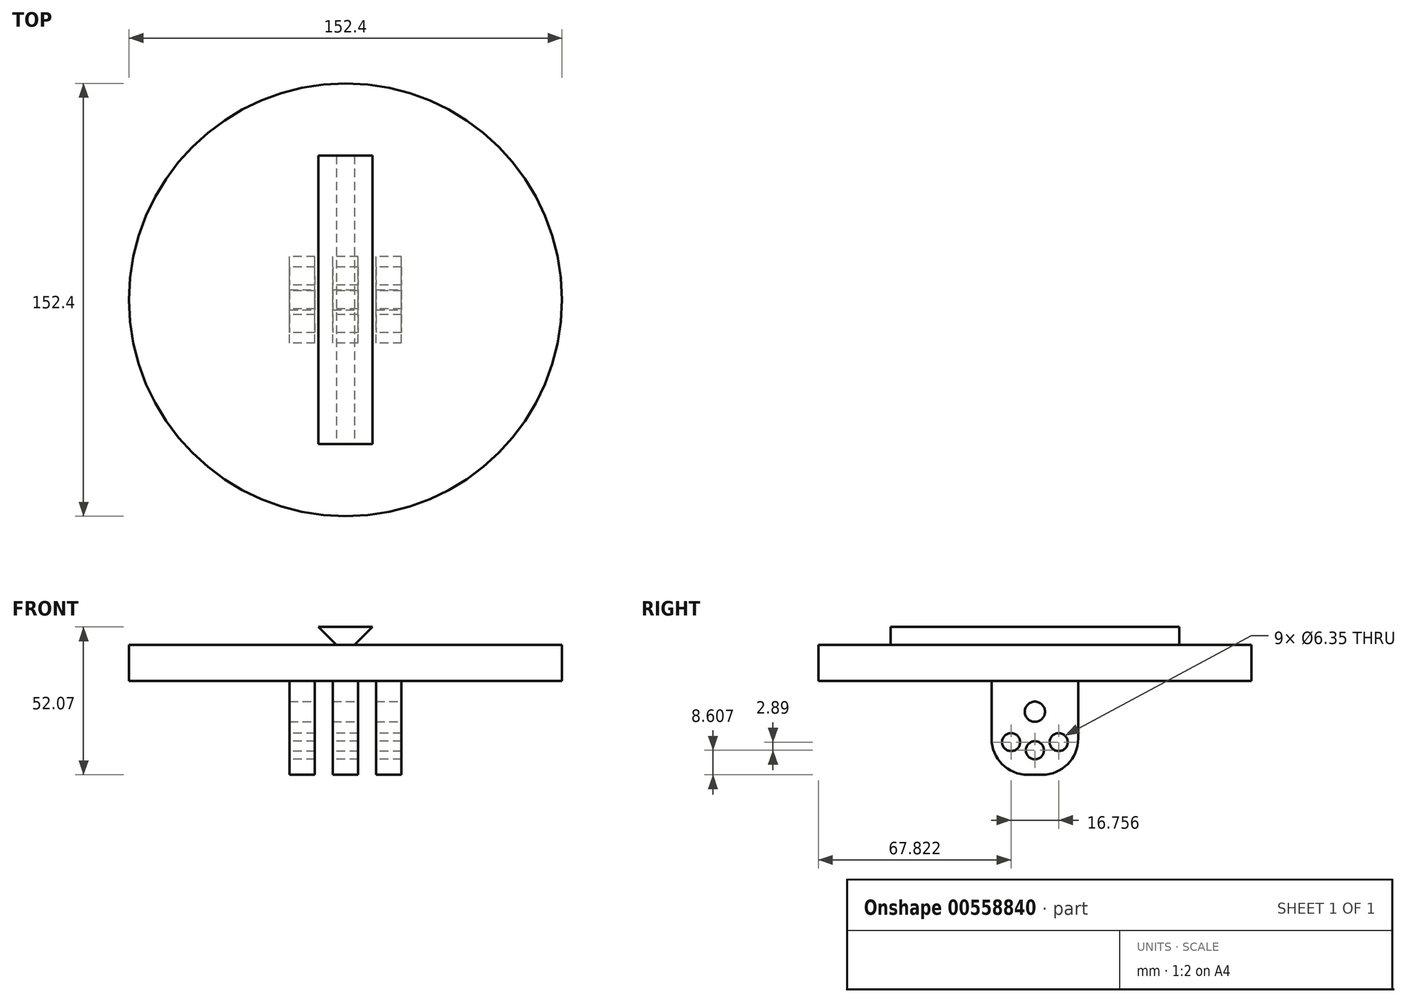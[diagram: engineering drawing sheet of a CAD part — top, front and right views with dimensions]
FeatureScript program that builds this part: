
annotation { "Feature Type Name" : "Feature", "Feature Type Description" : "" }
export const myFeature = defineFeature(function(context is Context, id is Id, definition is map)
    precondition{}
    {
        {
            var Q0;
            Q0=qCreatedBy(makeId("Top.planeOp"),FACE);
            var sketch = newSketch(context, id + "F0", { "sketchPlane" : qUnion([Q0])});
            skCircle(sketch, "E0", {"center": v(0, 0) * mm, "radius": 76.2 * mm});
            skSolve(sketch);
        }
        {
            var Q0;
            Q0=makeQuery(id+"F0.imprint","IMPRINT",FACE,{"disambiguationData":[TD([[makeQuery(id+"F0.imprint","IMPRINT",EDGE,{"derivedFrom":sQuery(id+"F0.wireOp",EDGE,"E0")}),1.0]])]});
            extrude(context, id + "F1", {"entities" : qUnion([Q0]), "depth" : 12.7 * mm, "offsetDistance" : 25.4 * mm});
        }
        {
            var Q0;
            Q0=makeQuery(id+"F1.opExtrude","CAP_FACE",FACE,{"disambiguationData":[OSD([sQuery(id+"F0.wireOp",EDGE,"E0")])],"isStart":false});
            var sketch = newSketch(context, id + "F2", { "sketchPlane" : qUnion([Q0])});
            skLineSegment(sketch, "E1.bottom", {"start": v(-9.53, 50.8) * mm, "end": v(9.53, 50.8) * mm});
            skLineSegment(sketch, "E1.top", {"start": v(-9.53, -50.8) * mm, "end": v(9.52, -50.8) * mm});
            skLineSegment(sketch, "E1.left", {"start": v(-9.53, 50.8) * mm, "end": v(-9.53, -50.8) * mm});
            skLineSegment(sketch, "E1.right", {"start": v(9.53, 50.8) * mm, "end": v(9.52, -50.8) * mm});
            skPoint(sketch, "E1.middle", {"position": v(0, 0) * mm});
            skSolve(sketch);
        }
        {
            var Q0;
            Q0=makeQuery(id+"F2.imprint","IMPRINT",FACE,{"disambiguationData":[TD([[makeQuery(id+"F2.imprint","IMPRINT",EDGE,{"derivedFrom":sQuery(id+"F2.wireOp",EDGE,"E1.bottom")}),-1.0]])]});
            extrude(context, id + "F3", {"entities" : qUnion([Q0]), "operationType" : NewBodyOperationType.ADD, "depth" : 6.35 * mm, "offsetDistance" : 25.4 * mm});
        }
        {
            var Q0;
            Q0=makeQuery(id+"F3.opExtrude","SWEPT_FACE",FACE,{"disambiguationData":[OSD([sQuery(id+"F2.wireOp",EDGE,"E1.top")])]});
            var sketch = newSketch(context, id + "F4", { "sketchPlane" : qUnion([Q0])});
            skLineSegment(sketch, "E2", {"start": v(-9.53, 19.05) * mm, "end": v(-3.18, 12.7) * mm});
            skLineSegment(sketch, "E3", {"start": v(9.52, 19.05) * mm, "end": v(3.17, 12.7) * mm});
            skSolve(sketch);
        }
        {
            var Q0;
            Q0 = qSketchRegion(id + "F4", true);
            var Q1;
            {var subQ0=sQuery(id+"F4.wireOp",EDGE,"E2");Q1=makeQuery(id+"F4.imprint","IMPRINT",FACE,{"disambiguationData":[TD([[makeQuery(id+"F4.imprint","IMPRINT",EDGE,{"derivedFrom":subQ0}),-1.0]])]});}
            var Q2;
            {var subQ0=sQuery(id+"F4.wireOp",EDGE,"E3");Q2=makeQuery(id+"F4.imprint","IMPRINT",FACE,{"disambiguationData":[TD([[makeQuery(id+"F4.imprint","IMPRINT",EDGE,{"derivedFrom":subQ0}),1.0]])]});}
            extrude(context, id + "F5", {"entities" : qUnion([Q0, Q1, Q2]), "operationType" : NewBodyOperationType.REMOVE, "endBound" : BoundingType.THROUGH_ALL, "oppositeDirection" : true, "depth" : 25.4 * mm, "offsetDistance" : 25.4 * mm});
        }
        {
            var Q0;
            Q0=makeQuery(id+"F1.opExtrude","CAP_FACE",FACE,{"disambiguationData":[OSD([sQuery(id+"F0.wireOp",EDGE,"E0")])],"isStart":true});
            var sketch = newSketch(context, id + "F6", { "sketchPlane" : qUnion([Q0])});
            skLineSegment(sketch, "E4.bottom", {"start": v(-10.8, 15.24) * mm, "end": v(-19.69, 15.24) * mm});
            skLineSegment(sketch, "E4.top", {"start": v(-10.8, -15.24) * mm, "end": v(-19.69, -15.24) * mm});
            skLineSegment(sketch, "E4.left", {"start": v(-10.8, 15.24) * mm, "end": v(-10.8, -15.24) * mm});
            skLineSegment(sketch, "E4.right", {"start": v(-19.69, 15.24) * mm, "end": v(-19.69, -15.24) * mm});
            skPoint(sketch, "E4.middle", {"position": v(-15.24, 0) * mm});
            skLineSegment(sketch, "E5.1.0.0", {"start": v(-4.45, 15.24) * mm, "end": v(-4.45, -15.24) * mm});
            skLineSegment(sketch, "E5.1.0.1", {"start": v(4.44, 15.24) * mm, "end": v(-4.45, 15.24) * mm});
            skLineSegment(sketch, "E5.1.0.2", {"start": v(4.44, 15.24) * mm, "end": v(4.44, -15.24) * mm});
            skLineSegment(sketch, "E5.1.0.3", {"start": v(4.44, -15.24) * mm, "end": v(-4.45, -15.24) * mm});
            skLineSegment(sketch, "E5.2.0.0", {"start": v(10.8, 15.24) * mm, "end": v(10.8, -15.24) * mm});
            skLineSegment(sketch, "E5.2.0.1", {"start": v(19.68, 15.24) * mm, "end": v(10.8, 15.24) * mm});
            skLineSegment(sketch, "E5.2.0.2", {"start": v(19.68, 15.24) * mm, "end": v(19.68, -15.24) * mm});
            skLineSegment(sketch, "E5.2.0.3", {"start": v(19.68, -15.24) * mm, "end": v(10.8, -15.24) * mm});
            skLineSegment(sketch, "E5.direction1", {"start": v(-19.69, -15.24) * mm, "end": v(-4.45, -15.24) * mm, "construction": true});
            skSolve(sketch);
        }
        {
            var Q0;
            Q0=makeQuery(id+"F6.imprint","IMPRINT",FACE,{"disambiguationData":[TD([[makeQuery(id+"F6.imprint","IMPRINT",EDGE,{"derivedFrom":sQuery(id+"F6.wireOp",EDGE,"E5.2.0.0")}),1.0]])]});
            var Q1;
            Q1=makeQuery(id+"F6.imprint","IMPRINT",FACE,{"disambiguationData":[TD([[makeQuery(id+"F6.imprint","IMPRINT",EDGE,{"derivedFrom":sQuery(id+"F6.wireOp",EDGE,"E5.1.0.0")}),1.0]])]});
            var Q2;
            Q2=makeQuery(id+"F6.imprint","IMPRINT",FACE,{"disambiguationData":[TD([[makeQuery(id+"F6.imprint","IMPRINT",EDGE,{"derivedFrom":sQuery(id+"F6.wireOp",EDGE,"E4.bottom")}),1.0]])]});
            extrude(context, id + "F7", {"entities" : qUnion([Q0, Q1, Q2]), "operationType" : NewBodyOperationType.ADD, "depth" : 33.02 * mm, "offsetDistance" : 25.4 * mm});
        }
        {
            var Q0;
            Q0=makeQuery(id+"F7.opExtrude","CAP_EDGE",EDGE,{"disambiguationData":[OSD([sQuery(id+"F6.wireOp",EDGE,"E4.bottom")])],"isStart":false});
            var Q1;
            Q1=makeQuery(id+"F7.opExtrude","CAP_EDGE",EDGE,{"disambiguationData":[OSD([sQuery(id+"F6.wireOp",EDGE,"E4.top")])],"isStart":false});
            var Q2;
            Q2=makeQuery(id+"F7.opExtrude","CAP_EDGE",EDGE,{"disambiguationData":[OSD([sQuery(id+"F6.wireOp",EDGE,"E5.1.0.1")])],"isStart":false});
            var Q3;
            Q3=makeQuery(id+"F7.opExtrude","CAP_EDGE",EDGE,{"disambiguationData":[OSD([sQuery(id+"F6.wireOp",EDGE,"E5.1.0.3")])],"isStart":false});
            var Q4;
            Q4=makeQuery(id+"F7.opExtrude","CAP_EDGE",EDGE,{"disambiguationData":[OSD([sQuery(id+"F6.wireOp",EDGE,"E5.2.0.3")])],"isStart":false});
            var Q5;
            Q5=makeQuery(id+"F7.opExtrude","CAP_EDGE",EDGE,{"disambiguationData":[OSD([sQuery(id+"F6.wireOp",EDGE,"E5.2.0.1")])],"isStart":false});
            fillet(context, id + "F8", {"entities" : qUnion([Q0, Q1, Q2, Q3, Q4, Q5]), "radius" : 12.7 * mm, "tangentPropagation" : true, "allowEdgeOverflow" : false});
        }
        {
            var Q0;
            Q0=makeQuery(id+"F7.opExtrude","SWEPT_FACE",FACE,{"disambiguationData":[OSD([sQuery(id+"F6.wireOp",EDGE,"E5.2.0.2")])]});
            var sketch = newSketch(context, id + "F9", { "sketchPlane" : qUnion([Q0])});
            skCircle(sketch, "E6", {"center": v(0, -10.82) * mm, "radius": 3.56 * mm});
            skSolve(sketch);
        }
        {
            var Q0;
            Q0=makeQuery(id+"F9.imprint","IMPRINT",FACE,{"disambiguationData":[TD([[makeQuery(id+"F9.imprint","IMPRINT",EDGE,{"derivedFrom":sQuery(id+"F9.wireOp",EDGE,"E6")}),1.0]])]});
            extrude(context, id + "F10", {"entities" : qUnion([Q0]), "operationType" : NewBodyOperationType.REMOVE, "endBound" : BoundingType.THROUGH_ALL, "oppositeDirection" : true, "depth" : 25.4 * mm, "offsetDistance" : 25.4 * mm});
        }
        {
            var Q0;
            Q0=makeQuery(id+"F7.opExtrude","SWEPT_FACE",FACE,{"disambiguationData":[OSD([sQuery(id+"F6.wireOp",EDGE,"E4.right")])]});
            var sketch = newSketch(context, id + "F11", { "sketchPlane" : qUnion([Q0])});
            skCircle(sketch, "E7", {"center": v(8.38, -21.52) * mm, "radius": 3.18 * mm});
            skCircle(sketch, "E8", {"center": v(-8.38, -21.52) * mm, "radius": 3.18 * mm});
            skCircle(sketch, "E9", {"center": v(0, -24.41) * mm, "radius": 3.18 * mm});
            skSolve(sketch);
        }
        {
            var Q0;
            Q0=makeQuery(id+"F11.imprint","IMPRINT",FACE,{"disambiguationData":[TD([[makeQuery(id+"F11.imprint","IMPRINT",EDGE,{"derivedFrom":sQuery(id+"F11.wireOp",EDGE,"E8")}),1.0]])]});
            var Q1;
            Q1=makeQuery(id+"F11.imprint","IMPRINT",FACE,{"disambiguationData":[TD([[makeQuery(id+"F11.imprint","IMPRINT",EDGE,{"derivedFrom":sQuery(id+"F11.wireOp",EDGE,"E9")}),1.0]])]});
            var Q2;
            Q2=makeQuery(id+"F11.imprint","IMPRINT",FACE,{"disambiguationData":[TD([[makeQuery(id+"F11.imprint","IMPRINT",EDGE,{"derivedFrom":sQuery(id+"F11.wireOp",EDGE,"E7")}),1.0]])]});
            extrude(context, id + "F12", {"entities" : qUnion([Q0, Q1, Q2]), "operationType" : NewBodyOperationType.REMOVE, "endBound" : BoundingType.THROUGH_ALL, "oppositeDirection" : true, "depth" : 25.4 * mm, "offsetDistance" : 25.4 * mm});
        }
    });
